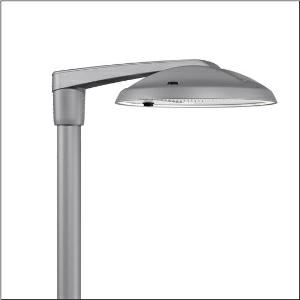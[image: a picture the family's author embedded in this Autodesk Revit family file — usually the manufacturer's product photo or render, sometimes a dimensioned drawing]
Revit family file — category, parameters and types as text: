
# Revit family: dl_r__50_iq_mini___st1_0a_5xa248d31y08le_5d77
name_source: partatom
category: Lighting Fixtures
units: mm (PartAtom-declared; Revit-internal decimal feet)

## family parameters
Cut with Voids When Loaded = No
Host = Face
Light Source = No
Part Type = Normal
Room Calculation Point = No
Round Connector Dimension = Use Diameter
Shared = No

## types (1)
- --- (1 x LED, 10390 lm, 66 W, 3000K)
    Apparent Load = 66 VA
    CIE Flux Codes = 37 72 97 100 100
    Color Rendering = 70
    Color Temperature = 3000K
    Default Elevation = 1800 mm
    Description = DL® 50 iQ mini, mast luminaire, primary light control with lens, of PMMA, primary optical cover: cover, of toughened safety glass, transparent, light distribution: ST1.0a, light emission: direct distribution, primary light characteristic: asymmetric, installation type: post-top, side-entry, LED, High Power LED, rated luminous flux: 10.390lm, luminous efficacy: 157lm/W, light colour: 730, colour temperature: 3000K, control: optimised constant luminous flux control (CLO 2.0), Desk-Remote (wireless, voltage-free reading and setting of iQ features in the workshop via application-optimized NFC function/RFID function), Light-Fading, Smart-Wire, Night-Set, Lumen-Switch, Temp-Guard, Auto-Match, Street-Remote, presetting dimming logarithmic, mains connection: 230..240V, AC, 50/60Hz, connection cable pre-assembled, cable length: 8,5m, start of lifetime: 66W, end of service life: 69W, reduction: 30W, luminaire housing, of diecast aluminium, powder-coated, Siteco® metallic grey (DB 702S), inclination adjustable: 0°, 5°, 10° (post-top) | 0°, -5°, -10°, -15° (side-entry), please order mast post-top element or mast side-entry element separately, diameter: 500mm, height: 115mm, post-top: for spigot size d x l = 76 x 100mm; with reducer (optional accessory) 60 x 100mm | side-entry: for spigot size d x l = 60 x 100mm; with reducer (optional accessory) 42 x 100mm, Smart Interface below and above, protection rating (complete): IP66, insulation class (complete): insulation class II (safety insulation), certification: CE, ENEC, VDE, impact resistance: IK08, permissible operating ambient temperature for outdoor applications: -25..+40°C, standard-compliant lighting for roads and squares, packaging unit: 1 piece

Light Distribution: ST1.0a
    Height = 115 mm
    Lamp = 1 x LED
    Lamp Light Flux = 10390 lm
    Lamp Power = 66 W
    Lamp count = 1
    Length = 500 mm
    Luminous efficacy = 157 lm/W
    Manufacturer = Siteco
    ModVariant = No
    Model = 5XA248D31Y08LE
    Number of Poles = 1
    OnlyDefault = Yes
    Power Factor = 1
    Product Name = DL® 50 iQ mini | ST1.0a
    Product group = mast luminaire | pylon top
    ProductGroupID = 6100
    Protection Class = Protection class II
    Protection Degree = IP 66
    RLX_Detail_Level = 1
    RLX_Emergency_Light_Flux = 0 lm
    RLX_Emergency_Type = 0
    RLX_Emergency_Type_DB = No
    RlxData = <blob elided: 106997 chars, md5=05a46d48>
    Socket = socket
    Standby Power = 0 W
    System Light Flux = 10390 lm
    System Power = 66 W
    Type Comments = factory setting: luminous flux: 100 % | dim-lin: 254 | 691 mA
    Type Image = l_1251786.jpg
    URL = http://relux.com
    VarID = @adj_024221
    Voltage = 0 V
    Weight = 0.00 kg
    Width = 0 mm  [stored 0 ft]

note: [stored X ft] marks values corroborated as IEEE doubles in the binary element streams (Revit-internal decimal feet)

## geometry (parser evidence)
native form markers: Blend x4, Sweep x11
no freeform markers — native parametric forms only
